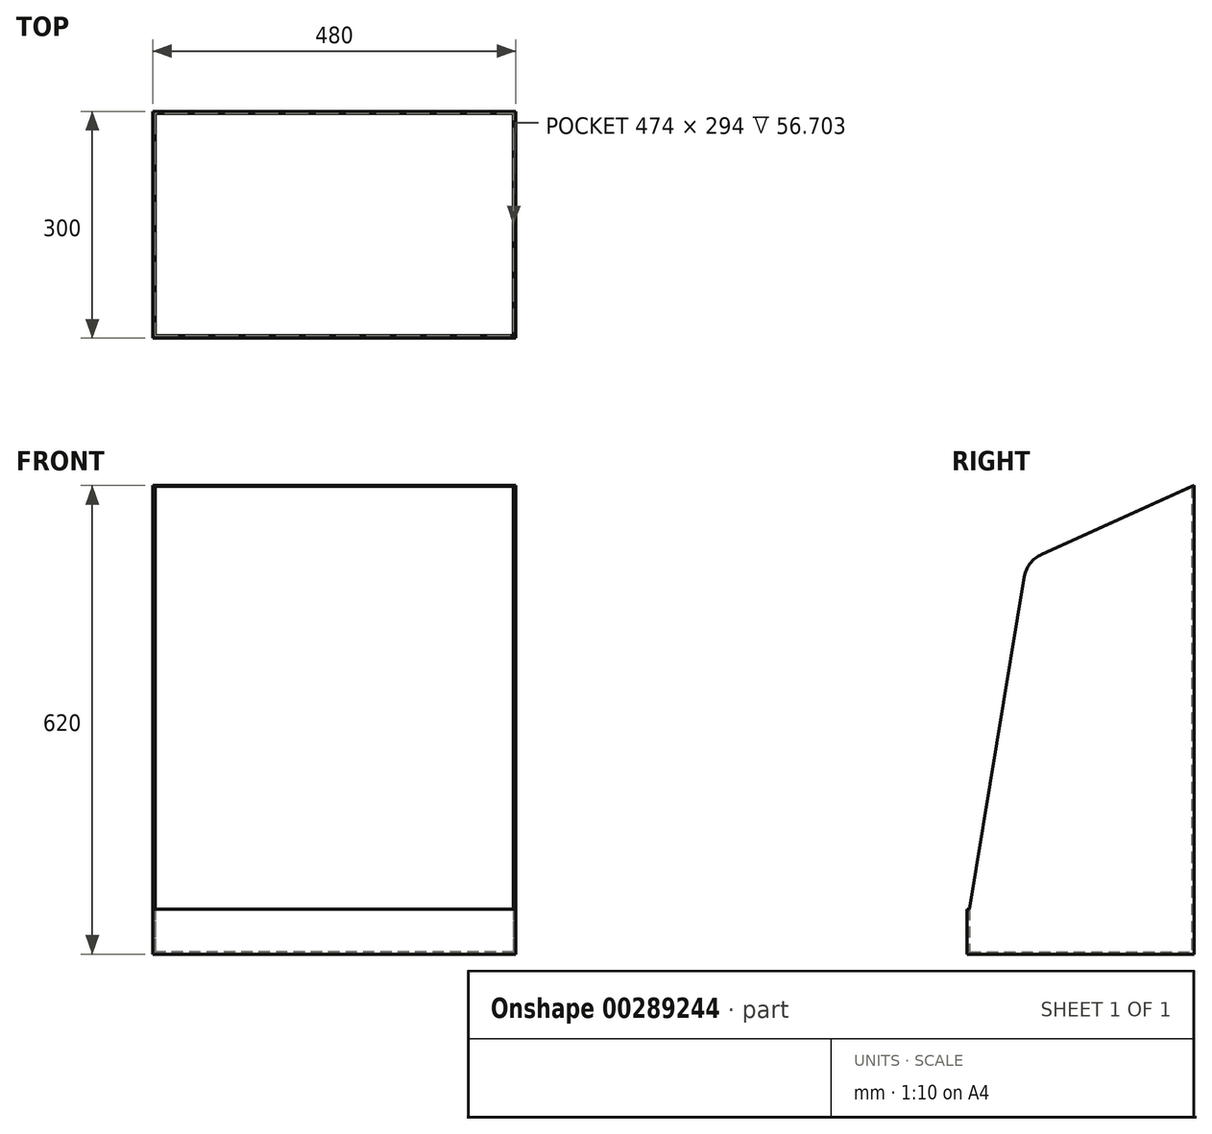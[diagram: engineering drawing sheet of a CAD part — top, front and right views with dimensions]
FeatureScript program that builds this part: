
annotation { "Feature Type Name" : "Feature", "Feature Type Description" : "" }
export const myFeature = defineFeature(function(context is Context, id is Id, definition is map)
    precondition{}
    {
        {
            var Q0;
            Q0=qCreatedBy(makeId("Top.planeOp"),FACE);
            var sketch = newSketch(context, id + "F0", { "sketchPlane" : qUnion([Q0])});
            skLineSegment(sketch, "E0.bottom", {"start": v(240, -150) * mm, "end": v(-240, -150) * mm});
            skLineSegment(sketch, "E0.top", {"start": v(240, 150) * mm, "end": v(-240, 150) * mm});
            skLineSegment(sketch, "E0.left", {"start": v(240, -150) * mm, "end": v(240, 150) * mm});
            skLineSegment(sketch, "E0.right", {"start": v(-240, -150) * mm, "end": v(-240, 150) * mm});
            skPoint(sketch, "E0.middle", {"position": v(0, 0) * mm});
            skSolve(sketch);
        }
        {
            var Q0;
            Q0=qSketchRegion(id+"F0",true);
            extrude(context, id + "F1", {"entities" : qUnion([Q0]), "depth" : 620 * mm});
        }
        {
            var Q0;
            Q0=makeQuery(id+"F1.opExtrude","CAP_FACE",FACE,{"disambiguationData":[OSD([sQuery(id+"F0.wireOp",EDGE,"E0.bottom"),sQuery(id+"F0.wireOp",EDGE,"E0.top"),sQuery(id+"F0.wireOp",EDGE,"E0.left"),sQuery(id+"F0.wireOp",EDGE,"E0.right")])],"isStart":false});
            shell(context, id + "F2", {"entities" : qUnion([Q0]), "thickness" : 3 * mm});
        }
        {
            var Q0;
            Q0=qCreatedBy(makeId("Right.planeOp"),FACE);
            var sketch = newSketch(context, id + "F3", { "sketchPlane" : qUnion([Q0])});
            skLineSegment(sketch, "E1.0.3", {"start": v(-150, 59.7) * mm, "end": v(-150, 0) * mm});
            skPoint(sketch, "E2.visualSharp", {"position": v(-71, 520) * mm});
            skPoint(sketch, "E1.0.2.end.orphan", {"position": v(-150, 620) * mm});
            skLineSegment(sketch, "E3", {"start": v(-150, 59.7) * mm, "end": v(-208.32, 59.7) * mm});
            skLineSegment(sketch, "E4", {"start": v(-208.32, 59.7) * mm, "end": v(-228.21, 668.39) * mm});
            skLineSegment(sketch, "E5", {"start": v(-228.21, 668.39) * mm, "end": v(136.1, 668.39) * mm});
            skLineSegment(sketch, "E6", {"start": v(136.1, 668.39) * mm, "end": v(150, 620) * mm});
            skPoint(sketch, "E1.0.1.start.orphan", {"position": v(150, 0) * mm});
            skLineSegment(sketch, "E7", {"start": v(-150, 59.7) * mm, "end": v(-147, 59.7) * mm});
            skLineSegment(sketch, "E8", {"start": v(-147, 59.7) * mm, "end": v(-74.49, 498.9) * mm});
            skLineSegment(sketch, "E9", {"start": v(-51.51, 528.82) * mm, "end": v(150, 620) * mm});
            skArc(sketch, "E10.filletArc", {"start": v(-51.51, 528.82) * mm, "mid": v(-66.75, 516.73) * mm, "end": v(-74.49, 498.9) * mm});
            skSolve(sketch);
        }
        {
            var Q0;
            Q0 = qSketchRegion(id + "F3", true);
            extrude(context, id + "F4", {"entities" : qUnion([Q0]), "operationType" : NewBodyOperationType.REMOVE, "endBound" : BoundingType.SYMMETRIC, "oppositeDirection" : true, "depth" : 724 * mm});
        }
    });
